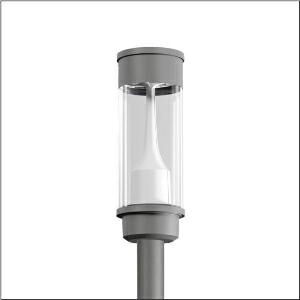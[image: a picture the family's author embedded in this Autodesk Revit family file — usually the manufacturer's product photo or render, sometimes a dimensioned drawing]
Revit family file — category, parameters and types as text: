
# Revit family: litepole_iq___pl1_2s_5xa5415jf14h000022_dba0
name_source: partatom
category: Lighting Fixtures
units: mm (PartAtom-declared; Revit-internal decimal feet)

## family parameters
Cut with Voids When Loaded = No
Host = Face
Light Source = No
Part Type = Normal
Room Calculation Point = No
Round Connector Dimension = Use Diameter
Shared = No

## types (1)
- --- (1 x LED, 2970 lm, 19.3 W, 3000K)
    Apparent Load = 19 VA
    CIE Flux Codes = 23 62 94 96 100
    Color Rendering = 70
    Color Temperature = 3000K
    Default Elevation = 1800 mm
    Description = Litepole iQ, mast luminaire, Module 540 iQ-SR, primary light control with 3 zone facetted reflector, of plastic, silver coated, highly specular, structured, primary optical cover: cover, of PMMA, transparent, light distribution: PL1.2s, light emission: direct distribution, primary light characteristic: symmetric, installation type: post-top, LED, High Power LED, rated luminous flux: 2.970lm, luminous efficacy: 154lm/W, light colour: 730, colour temperature: 3000K, control gear: iQ Street-Remote, control: Street-Remote, Auto-Match, Temp-Guard, Lumen-Switch, Night-Set, Smart-Wire, Light-Fading, Desk-Remote (wireless, voltage-free reading and setting of iQ features in the workshop via application-optimized NFC function/RFID function), optimised constant luminous flux control (CLO 2.0), pre-setting: logarithmic dimming characteristic, mains connection: 230..240V, AC, 50/60Hz, connection cable pre-assembled, cable length: 5,5m, wiring characteristics: H07RN-F, start of lifetime: 19W, end of service life: 21W, reduction: 10W, luminaire housing, upper part, of glass-fibre reinforced polyester, coated, SITECO metallic grey (DB 702S), diameter: 210mm, height: 590mm, spigot size: d x l = 76 x 70mm (post-top) | with reducer (optional accessory) 60 x 70mm, mounting height: 3..5m, post-top mast mounting element, of diecast aluminium, coated, SITECO metallic grey (DB 702S), Module 540 iQ-SR, traffic white (RAL 9016), equipment: standard, protection rating (complete): IP65, insulation class (complete): insulation class II (safety insulation), certification: CE, ENEC, VDE, packaging unit: 1 piece

Light Distribution: PL1.2s
    Height = 590 mm
    Lamp = 1 x LED
    Lamp Light Flux = 2970 lm
    Lamp Power = 19.3 W
    Lamp count = 1
    Length = 220 mm
    Luminous efficacy = 154 lm/W
    Manufacturer = Siteco
    ModVariant = No
    Model = 5XA5415JF14H000022
    Mounting Place = Pole
    Mounting Type = Pole top
    Number of Poles = 1
    OnlyDefault = Yes
    Power Factor = 1
    Product Name = Litepole iQ | PL1.2s
    Product group = mast luminaire | pylon top
    ProductGroupID = 6100
    Protection Class = Protection class II
    Protection Degree = IP 65
    RLX_Detail_Level = 1
    RLX_Emergency_Light_Flux = 0 lm
    RLX_Emergency_Type = 0
    RLX_Emergency_Type_DB = No
    RlxData = <blob elided: 40053 chars, md5=ed7b56f8>
    Socket = socket
    Standby Power = 0 W
    System Light Flux = 2970 lm
    System Power = 19 W
    Type Comments = factory setting: luminous flux: 100 % | dim-lin: 254 | 403 mA
    Type Image = l_1006025.jpg
    URL = http://relux.com
    VarID = @adj_145807
    Voltage = 0 V
    Weight = 0.00 kg
    Width = 0 mm  [stored 0 ft]

note: [stored X ft] marks values corroborated as IEEE doubles in the binary element streams (Revit-internal decimal feet)

## geometry (parser evidence)
native form markers: Blend x4, Sweep x10
no freeform markers — native parametric forms only
